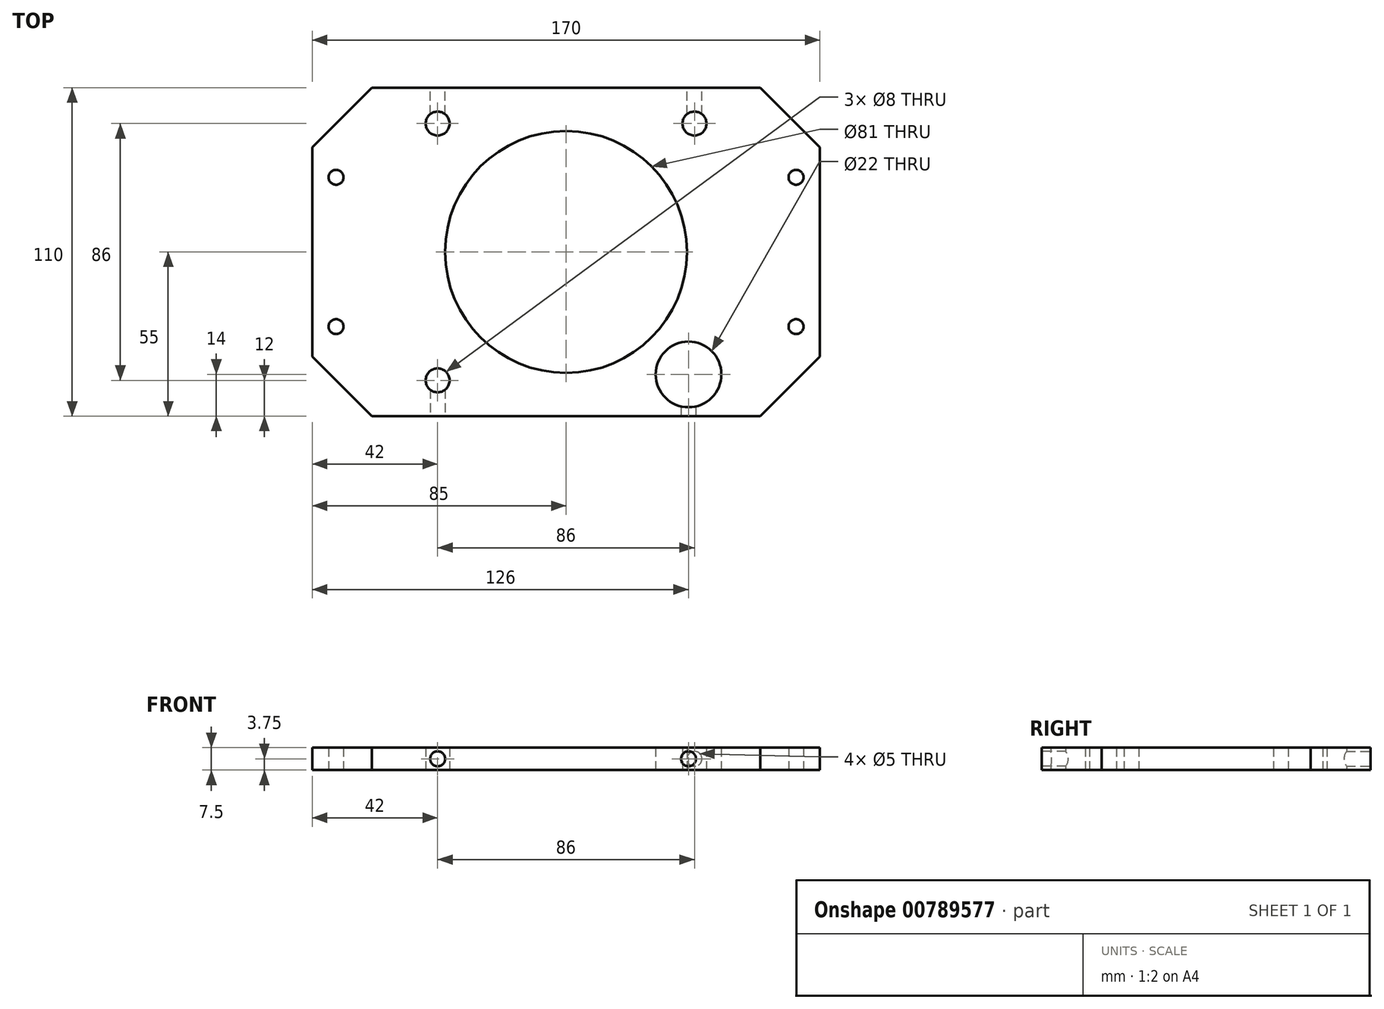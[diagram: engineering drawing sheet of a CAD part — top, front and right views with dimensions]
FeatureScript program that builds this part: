
annotation { "Feature Type Name" : "Feature", "Feature Type Description" : "" }
export const myFeature = defineFeature(function(context is Context, id is Id, definition is map)
    precondition{}
    {
        {
            var Q0;
            Q0=qCreatedBy(makeId("Top.planeOp"),FACE);
            var sketch = newSketch(context, id + "F0", { "sketchPlane" : qUnion([Q0])});
            skLineSegment(sketch, "E0.bottom", {"start": v(85, 55) * mm, "end": v(-85, 55) * mm});
            skLineSegment(sketch, "E0.top", {"start": v(85, -55) * mm, "end": v(-85, -55) * mm});
            skLineSegment(sketch, "E0.left", {"start": v(85, 55) * mm, "end": v(85, -55) * mm});
            skLineSegment(sketch, "E0.right", {"start": v(-85, 55) * mm, "end": v(-85, -55) * mm});
            skPoint(sketch, "E0.middle", {"position": v(0, 0) * mm});
            skCircle(sketch, "E1", {"center": v(0, 0) * mm, "radius": 40.5 * mm});
            skLineSegment(sketch, "E2", {"start": v(-85, -43) * mm, "end": v(-43, -43) * mm});
            skLineSegment(sketch, "E3", {"start": v(-43, -43) * mm, "end": v(-43, -55) * mm});
            skLineSegment(sketch, "E4", {"start": v(43, 55) * mm, "end": v(43, 43) * mm});
            skLineSegment(sketch, "E5", {"start": v(43, 43) * mm, "end": v(85, 43) * mm});
            skCircle(sketch, "E6", {"center": v(43, 43) * mm, "radius": 4 * mm});
            skCircle(sketch, "E7", {"center": v(-43, -43) * mm, "radius": 4 * mm});
            skLineSegment(sketch, "E8", {"start": v(41, -55) * mm, "end": v(41, -41) * mm});
            skLineSegment(sketch, "E9", {"start": v(-85, 43) * mm, "end": v(-43, 43) * mm});
            skLineSegment(sketch, "E10", {"start": v(-43, 43) * mm, "end": v(-43, 55) * mm});
            skCircle(sketch, "E11", {"center": v(-43, 43) * mm, "radius": 4 * mm});
            skCircle(sketch, "E12", {"center": v(41, -41) * mm, "radius": 11 * mm});
            skSolve(sketch);
        }
        {
            var Q0;
            Q0=makeQuery(id+"F0.imprint","IMPRINT",FACE,{"disambiguationData":[TD([[makeQuery(id+"F0.imprint","IMPRINT",EDGE,{"derivedFrom":sQuery(id+"F0.wireOp",EDGE,"E1")}),-1.0]])]});
            var Q1;
            {var subQ1=sQuery(id+"F0.wireOp",EDGE,"E0.left");var subQ6=sQuery(id+"F0.wireOp",EDGE,"E0.bottom");var subQ9=makeQuery(id+"F0.imprint","INTERSECT",VERTEX,{"derivedFrom":[subQ6,subQ1]});Q1=makeQuery(id+"F0.imprint","IMPRINT",FACE,{"disambiguationData":[TD([[makeQuery(id+"F0.imprint","IMPRINT",EDGE,{"disambiguationData":[TD([[subQ9,-1.0]])],"derivedFrom":subQ6}),1.0]])]});}
            var Q2;
            {var subQ1=sQuery(id+"F0.wireOp",EDGE,"E0.right");var subQ6=sQuery(id+"F0.wireOp",EDGE,"E0.top");var subQ9=makeQuery(id+"F0.imprint","INTERSECT",VERTEX,{"derivedFrom":[subQ6,subQ1]});Q2=makeQuery(id+"F0.imprint","IMPRINT",FACE,{"disambiguationData":[TD([[makeQuery(id+"F0.imprint","IMPRINT",EDGE,{"disambiguationData":[TD([[subQ9,1.0]])],"derivedFrom":subQ6}),-1.0]])]});}
            var Q3;
            {var subQ1=sQuery(id+"F0.wireOp",EDGE,"E0.right");var subQ6=sQuery(id+"F0.wireOp",EDGE,"E0.bottom");var subQ9=makeQuery(id+"F0.imprint","INTERSECT",VERTEX,{"derivedFrom":[subQ6,subQ1]});Q3=makeQuery(id+"F0.imprint","IMPRINT",FACE,{"disambiguationData":[TD([[makeQuery(id+"F0.imprint","IMPRINT",EDGE,{"disambiguationData":[TD([[subQ9,1.0]])],"derivedFrom":subQ6}),1.0]])]});}
            var Q4;
            {var subQ1=sQuery(id+"F0.wireOp",EDGE,"E4");var subQ11=sQuery(id+"F0.wireOp",EDGE,"E0.bottom");var subQ18=makeQuery(id+"F0.imprint","INTERSECT",VERTEX,{"derivedFrom":[subQ11,subQ1]});Q4=makeQuery(id+"F0.imprint","IMPRINT",FACE,{"disambiguationData":[TD([[makeQuery(id+"F0.imprint","IMPRINT",EDGE,{"disambiguationData":[TD([[subQ18,-1.0]])],"derivedFrom":subQ11}),1.0]])]});}
            var Q5;
            {var subQ0=sQuery(id+"F0.wireOp",EDGE,"E0.left");var subQ1=sQuery(id+"F0.wireOp",EDGE,"E0.top");var subQ2=makeQuery(id+"F0.imprint","INTERSECT",VERTEX,{"derivedFrom":[subQ1,subQ0]});Q5=makeQuery(id+"F0.imprint","IMPRINT",FACE,{"disambiguationData":[TD([[makeQuery(id+"F0.imprint","IMPRINT",EDGE,{"disambiguationData":[TD([[subQ2,-1.0]])],"derivedFrom":subQ1}),-1.0]])]});}
            var Q6;
            Q6=makeQuery(id+"F0.imprint","IMPRINT",FACE,{"disambiguationData":[TD([[makeQuery(id+"F0.imprint","IMPRINT",EDGE,{"derivedFrom":sQuery(id+"F0.wireOp",EDGE,"c5e99f40-eca4-49b6-b43b-0e23c1be7227")}),-1.0]])]});
            extrude(context, id + "F1", {"entities" : qUnion([Q0, Q1, Q2, Q3, Q4, Q5, Q6]), "depth" : 7.5 * mm, "offsetDistance" : 25 * mm});
        }
        {
            var Q0;
            Q0=makeQuery(id+"F1.opExtrude","CAP_FACE",FACE,{"disambiguationData":[OSD([sQuery(id+"F0.wireOp",EDGE,"E0.bottom"),sQuery(id+"F0.wireOp",EDGE,"E0.top"),sQuery(id+"F0.wireOp",EDGE,"E0.left"),sQuery(id+"F0.wireOp",EDGE,"E0.right"),sQuery(id+"F0.wireOp",EDGE,"E1"),sQuery(id+"F0.wireOp",EDGE,"E6"),sQuery(id+"F0.wireOp",EDGE,"E7")])],"isStart":true});
            var sketch = newSketch(context, id + "F2", { "sketchPlane" : qUnion([Q0])});
            skCircle(sketch, "E13", {"center": v(77, -25) * mm, "radius": 2.5 * mm});
            skCircle(sketch, "E14", {"center": v(-77, -25) * mm, "radius": 2.5 * mm});
            skCircle(sketch, "E15", {"center": v(77, 25) * mm, "radius": 2.5 * mm});
            skCircle(sketch, "E16", {"center": v(-77, 25) * mm, "radius": 2.5 * mm});
            skPoint(sketch, "E17", {"position": v(-43, -43) * mm});
            skPoint(sketch, "E18", {"position": v(-43, 43) * mm});
            skPoint(sketch, "E19", {"position": v(43, -43) * mm});
            skPoint(sketch, "E20", {"position": v(41, 41) * mm});
            skSolve(sketch);
        }
        {
            var Q0;
            Q0=makeQuery(id+"F1.opExtrude","SWEPT_EDGE",EDGE,{"disambiguationData":[OSD([sQuery(id+"F0.wireOp",EDGE,"E0.top"),sQuery(id+"F0.wireOp",EDGE,"E0.left")])]});
            var Q1;
            Q1=makeQuery(id+"F1.opExtrude","SWEPT_EDGE",EDGE,{"disambiguationData":[OSD([sQuery(id+"F0.wireOp",EDGE,"E0.top"),sQuery(id+"F0.wireOp",EDGE,"E0.right")])]});
            var Q2;
            Q2=makeQuery(id+"F1.opExtrude","SWEPT_EDGE",EDGE,{"disambiguationData":[OSD([sQuery(id+"F0.wireOp",EDGE,"E0.bottom"),sQuery(id+"F0.wireOp",EDGE,"E0.right")])]});
            var Q3;
            Q3=makeQuery(id+"F1.opExtrude","SWEPT_EDGE",EDGE,{"disambiguationData":[OSD([sQuery(id+"F0.wireOp",EDGE,"E0.bottom"),sQuery(id+"F0.wireOp",EDGE,"E0.left")])]});
            chamfer(context, id + "F3", {"entities" : qUnion([Q0, Q1, Q2, Q3]), "width" : 20 * mm, "tangentPropagation" : true});
        }
        {
            var Q0;
            Q0=makeQuery(id+"F2.imprint","IMPRINT",FACE,{"disambiguationData":[TD([[makeQuery(id+"F2.imprint","IMPRINT",EDGE,{"derivedFrom":sQuery(id+"F2.wireOp",EDGE,"E13")}),1.0]])]});
            var Q1;
            Q1=makeQuery(id+"F2.imprint","IMPRINT",FACE,{"disambiguationData":[TD([[makeQuery(id+"F2.imprint","IMPRINT",EDGE,{"derivedFrom":sQuery(id+"F2.wireOp",EDGE,"E15")}),1.0]])]});
            var Q2;
            Q2=makeQuery(id+"F2.imprint","IMPRINT",FACE,{"disambiguationData":[TD([[makeQuery(id+"F2.imprint","IMPRINT",EDGE,{"derivedFrom":sQuery(id+"F2.wireOp",EDGE,"E16")}),1.0]])]});
            var Q3;
            Q3=makeQuery(id+"F2.imprint","IMPRINT",FACE,{"disambiguationData":[TD([[makeQuery(id+"F2.imprint","IMPRINT",EDGE,{"derivedFrom":sQuery(id+"F2.wireOp",EDGE,"E14")}),1.0]])]});
            extrude(context, id + "F4", {"entities" : qUnion([Q0, Q1, Q2, Q3]), "operationType" : NewBodyOperationType.REMOVE, "oppositeDirection" : true, "depth" : 25 * mm, "offsetDistance" : 25 * mm});
        }
        {
            var Q0;
            Q0=makeQuery(id+"F1.opExtrude","SWEPT_FACE",FACE,{"disambiguationData":[OSD([sQuery(id+"F0.wireOp",EDGE,"E0.top")])]});
            var sketch = newSketch(context, id + "F5", { "sketchPlane" : qUnion([Q0])});
            skPoint(sketch, "E21", {"position": v(-43, 3.75) * mm});
            skPoint(sketch, "E21.positionSnap0", {"position": v(-65, 3.75) * mm});
            skPoint(sketch, "E22", {"position": v(41, 3.75) * mm});
            skCircle(sketch, "E23", {"center": v(41, 3.75) * mm, "radius": 2.5 * mm});
            skCircle(sketch, "E24", {"center": v(-43, 3.75) * mm, "radius": 2.5 * mm});
            skPoint(sketch, "E25", {"position": v(65, 3.75) * mm});
            skSolve(sketch);
        }
        {
            var Q0;
            Q0=makeQuery(id+"F5.imprint","IMPRINT",FACE,{"disambiguationData":[TD([[makeQuery(id+"F5.imprint","IMPRINT",EDGE,{"derivedFrom":sQuery(id+"F5.wireOp",EDGE,"E24")}),1.0]])]});
            var Q1;
            Q1=makeQuery(id+"F5.imprint","IMPRINT",FACE,{"disambiguationData":[TD([[makeQuery(id+"F5.imprint","IMPRINT",EDGE,{"derivedFrom":sQuery(id+"F5.wireOp",EDGE,"E23")}),1.0]])]});
            extrude(context, id + "F6", {"entities" : qUnion([Q0, Q1]), "operationType" : NewBodyOperationType.REMOVE, "oppositeDirection" : true, "depth" : 10 * mm, "offsetDistance" : 25 * mm});
        }
        {
            var Q0;
            Q0=makeQuery(id+"F1.opExtrude","SWEPT_FACE",FACE,{"disambiguationData":[OSD([sQuery(id+"F0.wireOp",EDGE,"E0.bottom")])]});
            var sketch = newSketch(context, id + "F7", { "sketchPlane" : qUnion([Q0])});
            skPoint(sketch, "E26", {"position": v(43, 3.75) * mm});
            skPoint(sketch, "E26.positionSnap0", {"position": v(65, 3.75) * mm});
            skPoint(sketch, "E27", {"position": v(-43, 3.75) * mm});
            skPoint(sketch, "E27.positionSnap0", {"position": v(-65, 3.75) * mm});
            skCircle(sketch, "E28", {"center": v(43, 3.75) * mm, "radius": 2.5 * mm});
            skCircle(sketch, "E29", {"center": v(-43, 3.75) * mm, "radius": 2.5 * mm});
            skSolve(sketch);
        }
        {
            var Q0;
            Q0=makeQuery(id+"F7.imprint","IMPRINT",FACE,{"disambiguationData":[TD([[makeQuery(id+"F7.imprint","IMPRINT",EDGE,{"derivedFrom":sQuery(id+"F7.wireOp",EDGE,"E29")}),1.0]])]});
            var Q1;
            Q1=makeQuery(id+"F7.imprint","IMPRINT",FACE,{"disambiguationData":[TD([[makeQuery(id+"F7.imprint","IMPRINT",EDGE,{"derivedFrom":sQuery(id+"F7.wireOp",EDGE,"E28")}),1.0]])]});
            extrude(context, id + "F8", {"entities" : qUnion([Q0, Q1]), "operationType" : NewBodyOperationType.REMOVE, "oppositeDirection" : true, "depth" : 10 * mm, "offsetDistance" : 25 * mm});
        }
    });
